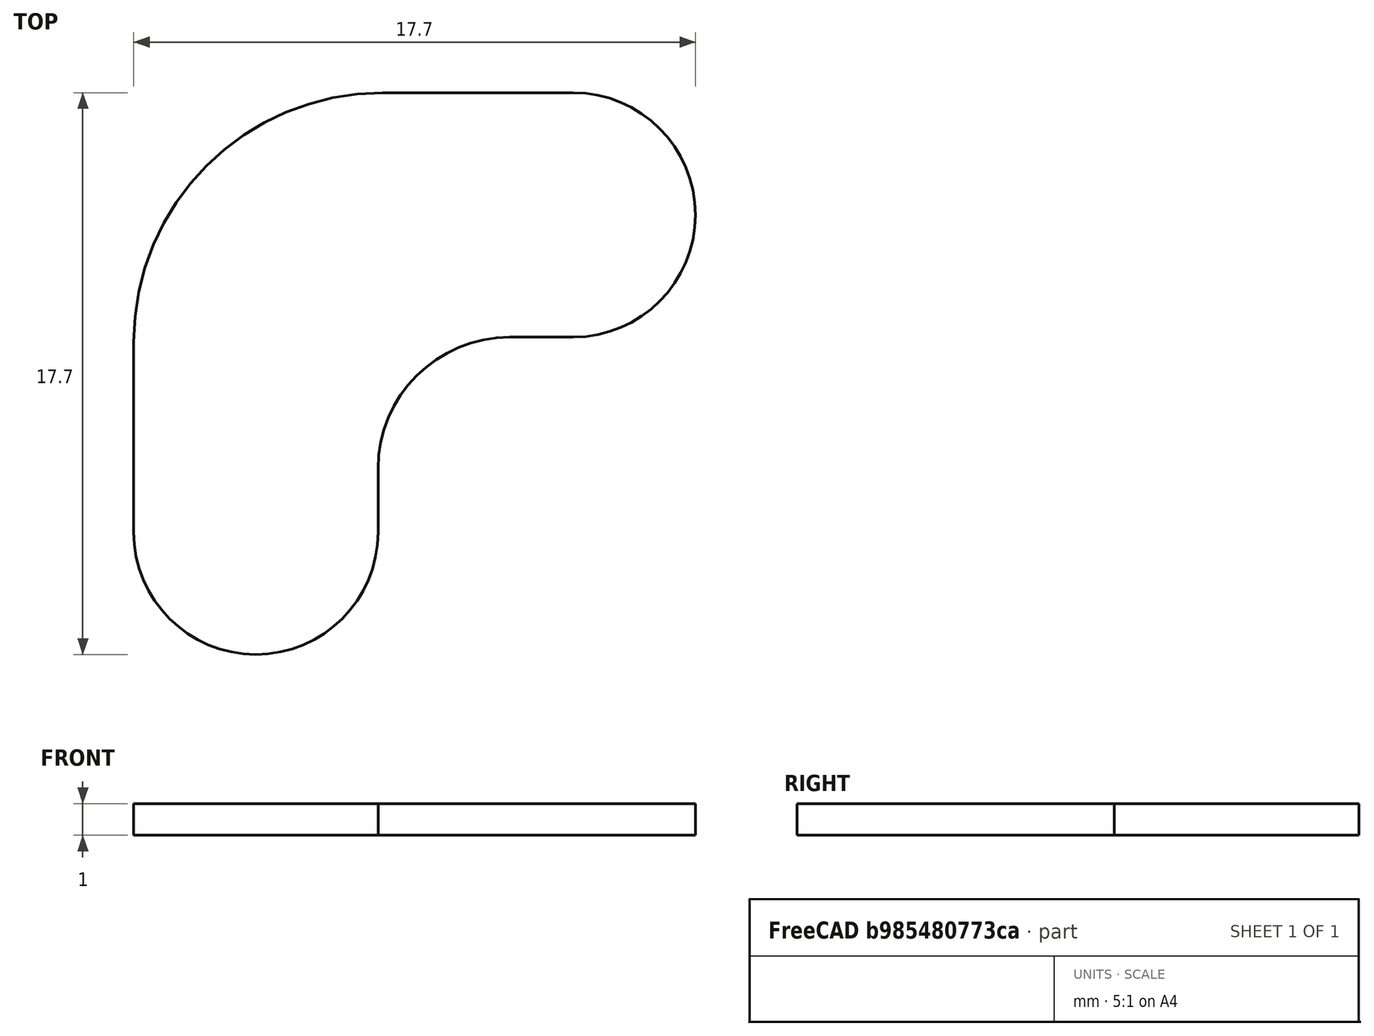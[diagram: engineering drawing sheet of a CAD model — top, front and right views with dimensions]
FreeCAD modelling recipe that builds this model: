
FCSTD DOCUMENT  (FreeCAD 1.0R39285 (Git))
Label: RUBBER-FOOT
License: All rights reserved
LicenseURL: https://en.wikipedia.org/wiki/All_rights_reserved
objects: TechDraw::DrawViewDimension×7, TechDraw::DrawViewPart×3, TechDraw::DrawHatch×3, PartDesign::Line×2, Sketcher::SketchObject×1, PartDesign::Pad×1, TechDraw::DrawSVGTemplate×1, TechDraw::DrawViewAnnotation×1, PartDesign::Plane×1, PartDesign::Body×1, TechDraw::DrawPage×1
note: 19 computed .brp shape members not serialized (recipe doc carries the construction recipe); baked Part::Feature solids carry a one-line shape summary decoded from their .brp

FEATURE [Sketcher::SketchObject] Sketch
  ArcFitTolerance = 0
  AttachmentSupport = -> [XY_Plane]
  FullyConstrained = true
  MakeInternals = false
  MapMode = 5
  sketch-geometry (10):
    g0: LineSegment StartX=-4.15 StartY=4.15 StartZ=0 EndX=-2.15 EndY=4.15 EndZ=0
    g1: LineSegment StartX=-2.15 StartY=11.85 StartZ=0 EndX=-8.15 EndY=11.85 EndZ=0
    g2: LineSegment StartX=-16 StartY=4 StartZ=0 EndX=-16 EndY=-2 EndZ=0
    g3: LineSegment StartX=-8.3 StartY=-7e-16 StartZ=0 EndX=-8.3 EndY=-2 EndZ=0
    g4: ArcOfCircle CenterX=-8.15 CenterY=4 CenterZ=0 NormalX=0 NormalY=0 NormalZ=1 AngleXU=0 Radius=7.85 StartAngle=1.5708 EndAngle=3.14159
    g5: ArcOfCircle CenterX=-4.15 CenterY=1.8645e-10 CenterZ=0 NormalX=0 NormalY=0 NormalZ=1 AngleXU=0 Radius=4.15 StartAngle=1.5708 EndAngle=3.14159
    g6: ArcOfCircle CenterX=-12.15 CenterY=-2 CenterZ=0 NormalX=0 NormalY=0 NormalZ=1 AngleXU=0 Radius=3.85 StartAngle=3.14159 EndAngle=6.28319
    g7: ArcOfCircle CenterX=-2.15 CenterY=8 CenterZ=0 NormalX=0 NormalY=0 NormalZ=1 AngleXU=0 Radius=3.85 StartAngle=4.71239 EndAngle=7.85398
    g8: GeomPoint [constr] X=1.7 Y=8 Z=0
    g9: GeomPoint [constr] X=-12.15 Y=-5.85 Z=0
  constraints (24):
    c: Horizontal(g0)
    c: Horizontal(g1)
    c: Vertical(g2)
    c: Tangent(g1,g4) = -1.5708
    c: Tangent(g2,g4) = -1.5708
    c: Tangent(g0,g5) = 1.5708
    c: Tangent(g3,g5) = -1.5708
    c: DistanceX(g2,g3) = 7.7
    c: Radius(g4) = 7.85
    c: Vertical(g3)
    c: Radius(g5) = 4.15
    c: Tangent(g7,g1) = -1.5708
    c: Tangent(g7,g0) = -1.5708
    c: Tangent(g6,g3) = 1.5708
    c: Tangent(g6,g2) = -1.5708
    c: PointOnObject(g8,g7)
    c: Horizontal(g7,g8)
    c: PointOnObject(g9,g6)
    c: Vertical(g6,g9)
    c: DistanceY(g9,g1) = 17.7
    c: DistanceX(g2,g8) = 17.7
    c: Radius(g7) = 3.85
    c: PointOnObject(g-1,g5)
    c: Horizontal(g-1,g3)
FEATURE [PartDesign::Pad] Pad
  Direction = (0,0,1)
  Length = 1
  Length2 = 10
  Profile = -> Sketch
  ReferenceAxis = -> Sketch [N_Axis]
  Suppressed = false
  Type = 0
FEATURE [TechDraw::DrawSVGTemplate] Template
  EditableTexts = COLOR=Black - RAL code: 9004; CreationDate=2023/12/07; E.G.APPROVED=APPROVED; FC-Scale=5:1; FC-Title=RUBBER-FOOT; IntechStudioLtd.=Intech Studio Ltd.; MATERIAL=Silicon or rubber; REV=02; STANDARD=DIN 16742-TG4
  Height = 297
  Orientation = 1
  Template = <userpath>/Desktop/A3_LandscapeTD_MODIFIED.svg
  Width = 420
FEATURE [TechDraw::DrawViewAnnotation] Annotation
  Font = osifont
  LineSpace = 100
  LockPosition = false
  MaxWidth = -1
  Rotation = 0
  ScaleType = 0
  Text = Self-adhesive on one side | Other side is aesthetical
  TextSize = 5
  TextStyle = 0
  X = 113.346
  Y = 98.3157
FEATURE [PartDesign::Plane] Plane_1
  AttachmentSupport = -> [Pad]
  Length = 100
  ResizeMode = 1
  Width = 100
FEATURE [PartDesign::Line] CircleAxis_1
  AttacherType = Attacher::AttachEngineLine
  AttachmentSupport = -> [Pad]
  Length = 17.1927
  MapMode = 19
  Placement = pos=(-2.15,8,1) rot=(0,0,-1;1.5708rad)
  ResizeMode = 1
FEATURE [PartDesign::Line] CircleAxis_2
  AttacherType = Attacher::AttachEngineLine
  AttachmentSupport = -> [Pad]
  Length = 17.1927
  MapMode = 19
  Placement = pos=(-12.15,-2,1) rot=(0,0,1;3.14159rad)
  ResizeMode = 1
FEATURE [PartDesign::Body] Body  label="RUBBER-FOOT"
  AllowCompound = false
  Group = -> [Sketch,Pad,Plane_1,CircleAxis_1,CircleAxis_2]
  Origin = -> Origin
  Tip = -> Pad
FEATURE [TechDraw::DrawViewPart] View
  CoarseView = false
  Direction = (0,0,1)
  Focus = 100
  HardHidden = true
  IsoCount = 0
  IsoHidden = false
  IsoVisible = false
  LockPosition = false
  Perspective = false
  Rotation = 0
  Scale = 5
  ScaleType = 2
  ScrubCount = 0
  SeamHidden = false
  SeamVisible = true
  SmoothHidden = false
  SmoothVisible = true
  Source = -> [Body]
  X = 117.879
  XDirection = (1,0,0)
  Y = 186.048
FEATURE [TechDraw::DrawViewPart] View001
  CoarseView = false
  Direction = (-1,0,0)
  Focus = 100
  HardHidden = true
  IsoCount = 0
  IsoHidden = false
  IsoVisible = false
  LockPosition = false
  Perspective = false
  Rotation = 0
  Scale = 5
  ScaleType = 2
  ScrubCount = 0
  SeamHidden = false
  SeamVisible = true
  SmoothHidden = false
  SmoothVisible = true
  Source = -> [Body]
  X = 261.925
  XDirection = (0,0,1)
  Y = 188.134
FEATURE [TechDraw::DrawViewPart] View002
  CoarseView = false
  Direction = (0.57735,0.57735,0.57735)
  Focus = 100
  HardHidden = true
  IsoCount = 0
  IsoHidden = false
  IsoVisible = false
  LockPosition = false
  Perspective = false
  Rotation = 0
  Scale = 5
  ScaleType = 2
  ScrubCount = 0
  SeamHidden = false
  SeamVisible = true
  SmoothHidden = false
  SmoothVisible = true
  Source = -> [Body]
  X = 364.506
  XDirection = (0.707107,0,-0.707107)
  Y = 231.154
FEATURE [TechDraw::DrawHatch] Hatch  label="HatchF1"
  HatchPattern = C:/Program Files/FreeCAD 0.21/data/Mod/TechDraw/Patterns/solid.svg
  Source = -> View002 [Face1]
FEATURE [TechDraw::DrawHatch] Hatch001  label="Hatch001F4"
  HatchPattern = C:/Program Files/FreeCAD 0.21/data/Mod/TechDraw/Patterns/solid.svg
  Source = -> View002 [Face4]
FEATURE [TechDraw::DrawHatch] Hatch002  label="Hatch002F3"
  HatchPattern = C:/Program Files/FreeCAD 0.21/data/Mod/TechDraw/Patterns/solid.svg
  Source = -> View002 [Face3,Face2,Face6,Face7,Face5]
FEATURE [TechDraw::DrawViewDimension] Dimension
  AngleOverride = false
  Arbitrary = false
  ArbitraryTolerances = false
  EqualTolerance = false
  ExtensionAngle = 0
  FormatSpec = %.2w
  FormatSpecOverTolerance = %+.2w
  FormatSpecUnderTolerance = %+.2w
  Inverted = false
  LineAngle = 0
  LockPosition = false
  MeasureType = 1
  OverTolerance = 0
  References2D = -> [View]
  Rotation = 0
  ScaleType = 0
  TheoreticalExact = false
  Type = 1
  UnderTolerance = -0.5
  X = -0.788548
  Y = 62.3415
FEATURE [TechDraw::DrawViewDimension] Dimension001
  AngleOverride = false
  Arbitrary = false
  ArbitraryTolerances = false
  EqualTolerance = false
  ExtensionAngle = 0
  FormatSpec = %.2w
  FormatSpecOverTolerance = %+.2w
  FormatSpecUnderTolerance = %+.2w
  Inverted = false
  LineAngle = 0
  LockPosition = false
  MeasureType = 1
  OverTolerance = 0
  References2D = -> [View]
  Rotation = 0
  ScaleType = 0
  TheoreticalExact = false
  Type = 2
  UnderTolerance = -0.5
  X = -65.1003
  Y = 3.4233
FEATURE [TechDraw::DrawViewDimension] Dimension002
  AngleOverride = false
  Arbitrary = false
  ArbitraryTolerances = false
  EqualTolerance = true
  ExtensionAngle = 0
  FormatSpec = R%.2w
  FormatSpecOverTolerance = %+.2w
  FormatSpecUnderTolerance = %+.2w
  Inverted = false
  LineAngle = 0
  LockPosition = false
  MeasureType = 1
  OverTolerance = 0
  References2D = -> [View]
  Rotation = 0
  ScaleType = 0
  TheoreticalExact = false
  Type = 4
  UnderTolerance = 0
  X = 8.94427
  Y = -2.89374
FEATURE [TechDraw::DrawViewDimension] Dimension003
  AngleOverride = false
  Arbitrary = false
  ArbitraryTolerances = false
  EqualTolerance = true
  ExtensionAngle = 0
  FormatSpec = R%.2w
  FormatSpecOverTolerance = %+.2w
  FormatSpecUnderTolerance = %+.2w
  Inverted = false
  LineAngle = 0
  LockPosition = false
  MeasureType = 1
  OverTolerance = 0
  References2D = -> [View]
  Rotation = 0
  ScaleType = 0
  TheoreticalExact = false
  Type = 4
  UnderTolerance = 0
  X = -56.5573
  Y = 68.9744
FEATURE [TechDraw::DrawViewDimension] Dimension004
  AngleOverride = false
  Arbitrary = false
  ArbitraryTolerances = false
  EqualTolerance = true
  ExtensionAngle = 0
  FormatSpec = 2x R%.2w
  FormatSpecOverTolerance = %+.2w
  FormatSpecUnderTolerance = %+.2w
  Inverted = false
  LineAngle = 0
  LockPosition = false
  MeasureType = 1
  OverTolerance = 0
  References2D = -> [View]
  Rotation = 0
  ScaleType = 0
  TheoreticalExact = false
  Type = 4
  UnderTolerance = 0
  X = 63.0908
  Y = 42.9779
FEATURE [TechDraw::DrawViewDimension] Dimension005
  AngleOverride = false
  Arbitrary = false
  ArbitraryTolerances = false
  EqualTolerance = false
  ExtensionAngle = 0
  FormatSpec = 2x %.2w
  FormatSpecOverTolerance = %+.2w
  FormatSpecUnderTolerance = %+.2w
  Inverted = false
  LineAngle = 0
  LockPosition = false
  MeasureType = 1
  OverTolerance = 0
  References2D = -> [View]
  Rotation = 0
  ScaleType = 0
  TheoreticalExact = false
  Type = 1
  UnderTolerance = -0.5
  X = -25
  Y = -58.5708
FEATURE [TechDraw::DrawViewDimension] Dimension006
  AngleOverride = false
  Arbitrary = false
  ArbitraryTolerances = false
  EqualTolerance = true
  ExtensionAngle = 0
  FormatSpec = %.2w
  FormatSpecOverTolerance = %+.2w
  FormatSpecUnderTolerance = %+.2w
  Inverted = false
  LineAngle = 0
  LockPosition = false
  MeasureType = 1
  OverTolerance = 0
  References2D = -> [View001]
  Rotation = 0
  ScaleType = 0
  TheoreticalExact = false
  Type = 1
  UnderTolerance = 0
  X = 8.85411
  Y = 61.7117
FEATURE [TechDraw::DrawPage] Page  label="RUBBER-FOOT_Drawing"
  KeepUpdated = true
  NextBalloonIndex = 3
  ProjectionType = 0
  Template = -> Template
  Views = -> [View,View001,View002,Dimension,Dimension001,Dimension002,Dimension003,Dimension004,Dimension005,Dimension006,Annotation]
